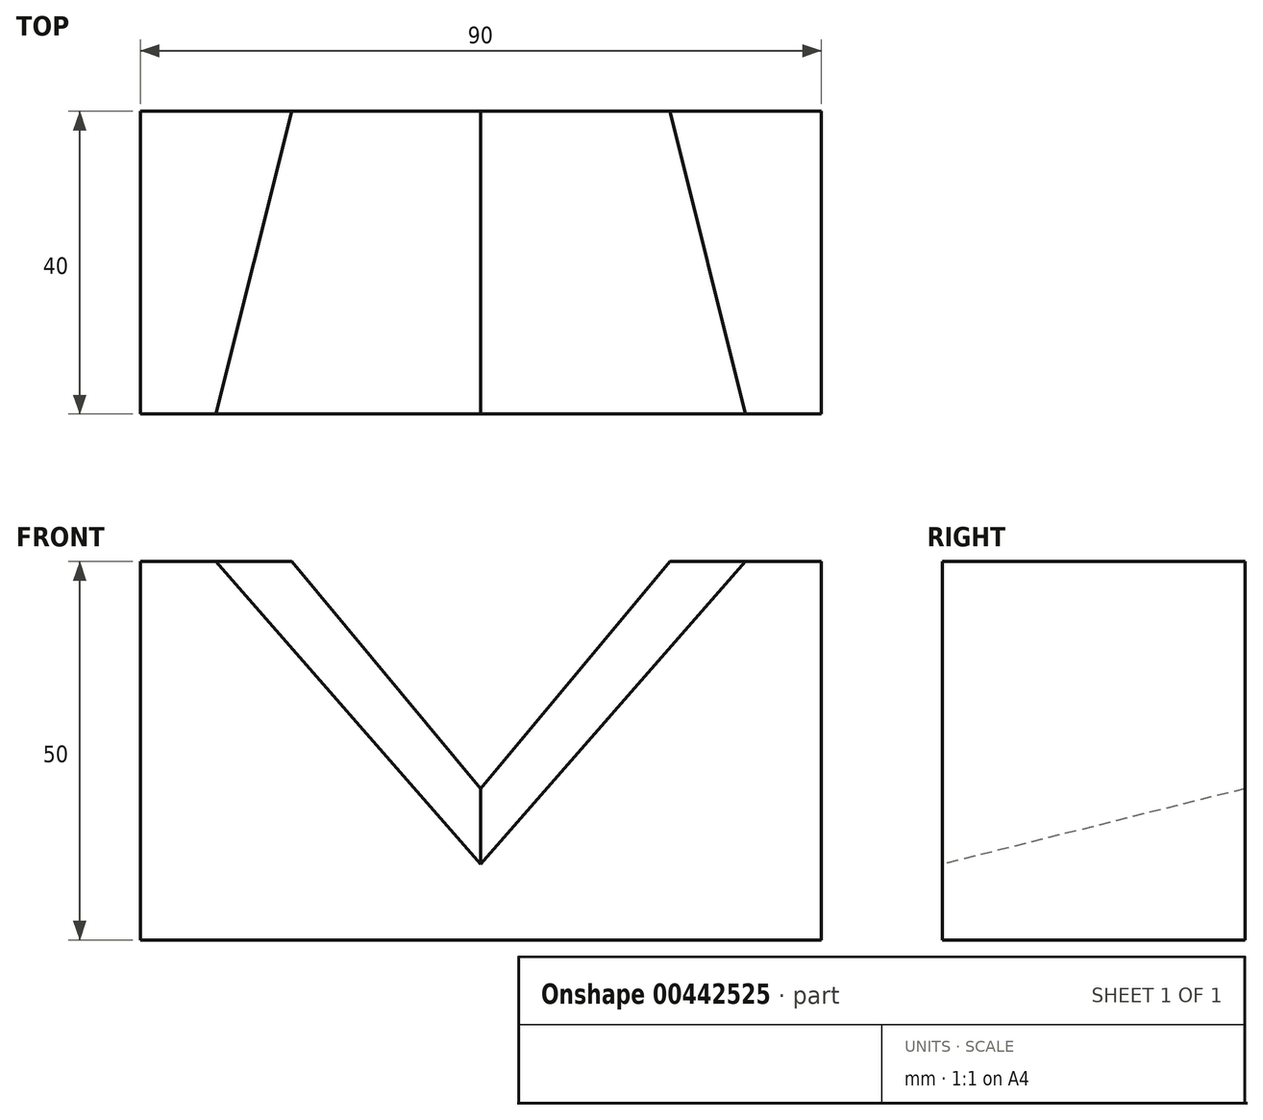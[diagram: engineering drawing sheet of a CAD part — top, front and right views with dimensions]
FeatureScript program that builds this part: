
annotation { "Feature Type Name" : "Feature", "Feature Type Description" : "" }
export const myFeature = defineFeature(function(context is Context, id is Id, definition is map)
    precondition{}
    {
        {
            var Q0;
            Q0=qCreatedBy(makeId("Front.planeOp"),FACE);
            var sketch = newSketch(context, id + "F0", { "sketchPlane" : qUnion([Q0])});
            skLineSegment(sketch, "E0.bottom", {"start": v(0, 0) * mm, "end": v(90, 0) * mm});
            skLineSegment(sketch, "E0.top", {"start": v(0, 50) * mm, "end": v(90, 50) * mm});
            skLineSegment(sketch, "E0.left", {"start": v(0, 0) * mm, "end": v(0, 50) * mm});
            skLineSegment(sketch, "E0.right", {"start": v(90, 0) * mm, "end": v(90, 50) * mm});
            skSolve(sketch);
        }
        {
            var Q0;
            Q0=makeQuery(id+"F0.imprint","IMPRINT",FACE,{"disambiguationData":[TD([[makeQuery(id+"F0.imprint","IMPRINT",EDGE,{"derivedFrom":sQuery(id+"F0.wireOp",EDGE,"E0.bottom")}),1.0]])]});
            extrude(context, id + "F1", {"entities" : qUnion([Q0]), "depth" : 40 * mm});
        }
        {
            var Q0;
            Q0=makeQuery(id+"F1.opExtrude","CAP_FACE",FACE,{"disambiguationData":[OSD([sQuery(id+"F0.wireOp",EDGE,"E0.bottom"),sQuery(id+"F0.wireOp",EDGE,"E0.top"),sQuery(id+"F0.wireOp",EDGE,"E0.left"),sQuery(id+"F0.wireOp",EDGE,"E0.right")])],"isStart":false});
            var sketch = newSketch(context, id + "F2", { "sketchPlane" : qUnion([Q0])});
            skLineSegment(sketch, "E1", {"start": v(10, 50) * mm, "end": v(45, 10) * mm});
            skLineSegment(sketch, "E2", {"start": v(45, 10) * mm, "end": v(80, 50) * mm});
            skLineSegment(sketch, "E3", {"start": v(80, 50) * mm, "end": v(10, 50) * mm});
            skSolve(sketch);
        }
        {
            var Q0;
            Q0=makeQuery(id+"F1.opExtrude","CAP_FACE",FACE,{"disambiguationData":[OSD([sQuery(id+"F0.wireOp",EDGE,"E0.bottom"),sQuery(id+"F0.wireOp",EDGE,"E0.top"),sQuery(id+"F0.wireOp",EDGE,"E0.left"),sQuery(id+"F0.wireOp",EDGE,"E0.right")])],"isStart":true});
            var sketch = newSketch(context, id + "F3", { "sketchPlane" : qUnion([Q0])});
            skLineSegment(sketch, "E4", {"start": v(-70, 50) * mm, "end": v(-45, 20) * mm});
            skLineSegment(sketch, "E5", {"start": v(-45, 20) * mm, "end": v(-20, 50) * mm});
            skLineSegment(sketch, "E6", {"start": v(-20, 50) * mm, "end": v(-70, 50) * mm});
            skSolve(sketch);
        }
        {
            var Q1;
            Q1=makeQuery(id+"F3.imprint","IMPRINT",FACE,{"disambiguationData":[TD([[makeQuery(id+"F3.imprint","IMPRINT",EDGE,{"derivedFrom":sQuery(id+"F3.wireOp",EDGE,"E4")}),1.0]])]});
            var Q2;
            Q2=makeQuery(id+"F2.imprint","IMPRINT",FACE,{"disambiguationData":[TD([[makeQuery(id+"F2.imprint","IMPRINT",EDGE,{"derivedFrom":sQuery(id+"F2.wireOp",EDGE,"E1")}),1.0]])]});
            loft(context, id + "F4", {"operationType" : NewBodyOperationType.REMOVE, "sheetProfilesArray" : [{ "sheetProfileEntities" : qUnion([Q1]) }, { "sheetProfileEntities" : qUnion([Q2]) }]});
        }
    });
